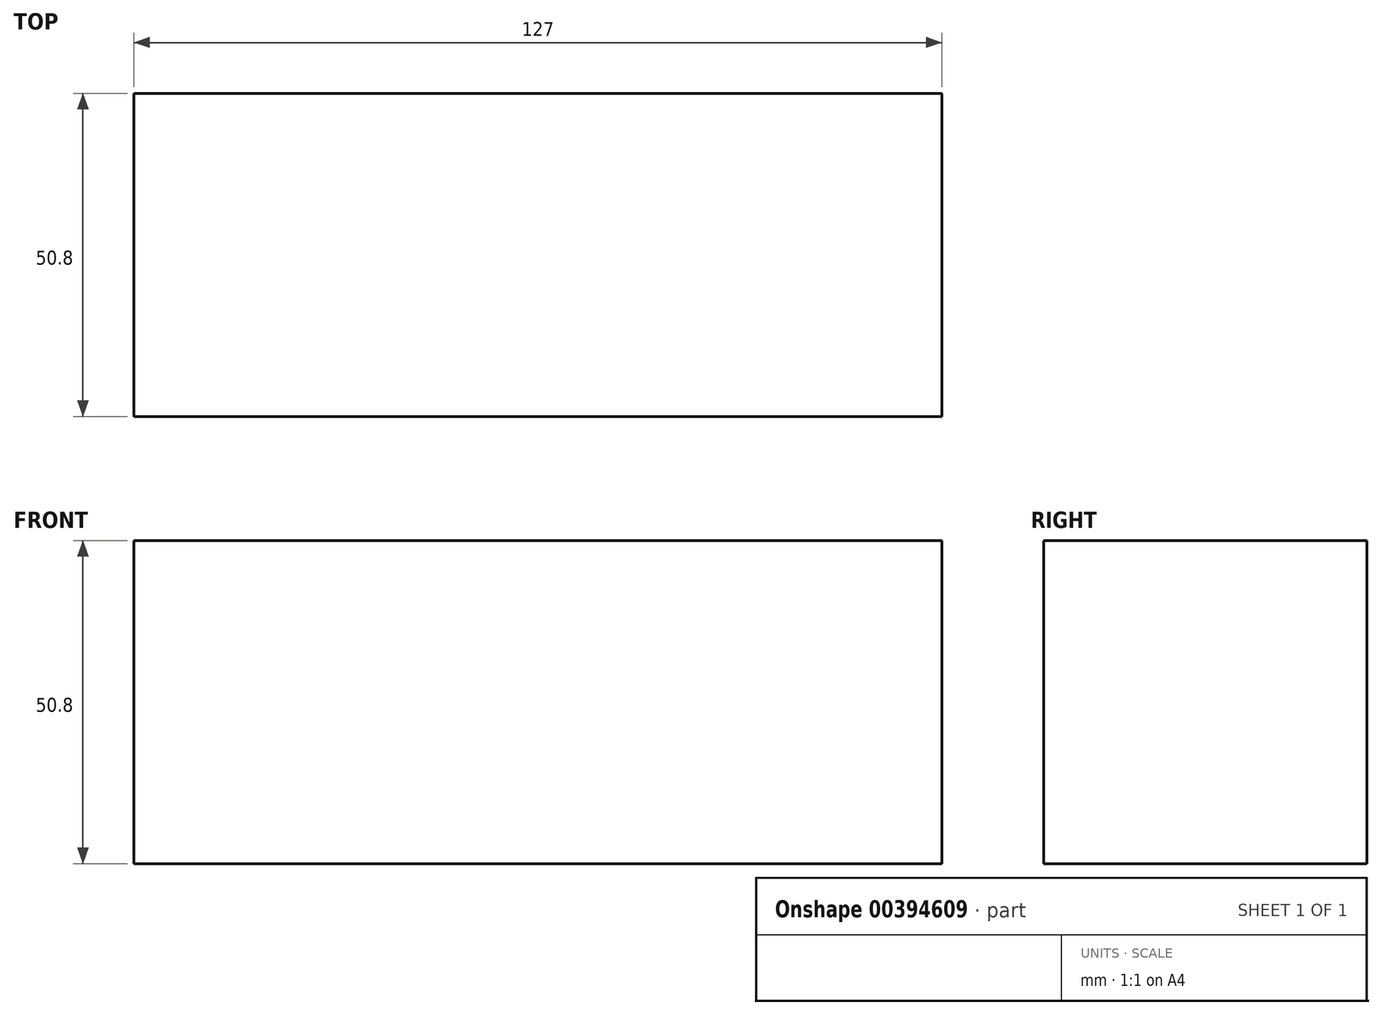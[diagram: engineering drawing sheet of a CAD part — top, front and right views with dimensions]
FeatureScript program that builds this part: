
annotation { "Feature Type Name" : "Feature", "Feature Type Description" : "" }
export const myFeature = defineFeature(function(context is Context, id is Id, definition is map)
    precondition{}
    {
        {
            var Q0;
            Q0=qCreatedBy(makeId("Front.planeOp"),FACE);
            var sketch = newSketch(context, id + "F0", { "sketchPlane" : qUnion([Q0])});
            skLineSegment(sketch, "E0.bottom", {"start": v(-63.22, 17.47) * mm, "end": v(63.78, 17.47) * mm});
            skLineSegment(sketch, "E0.top", {"start": v(-63.22, -33.33) * mm, "end": v(63.78, -33.33) * mm});
            skLineSegment(sketch, "E0.left", {"start": v(-63.22, 17.47) * mm, "end": v(-63.22, -33.33) * mm});
            skLineSegment(sketch, "E0.right", {"start": v(63.78, 17.47) * mm, "end": v(63.78, -33.33) * mm});
            skSolve(sketch);
        }
        {
            var Q0;
            Q0=makeQuery(id+"F0.imprint","IMPRINT",FACE,{"disambiguationData":[TD([[makeQuery(id+"F0.imprint","IMPRINT",EDGE,{"derivedFrom":sQuery(id+"F0.wireOp",EDGE,"E0.bottom")}),-1.0]])]});
            extrude(context, id + "F1", {"entities" : qUnion([Q0]), "depth" : 50.8 * mm});
        }
    });
